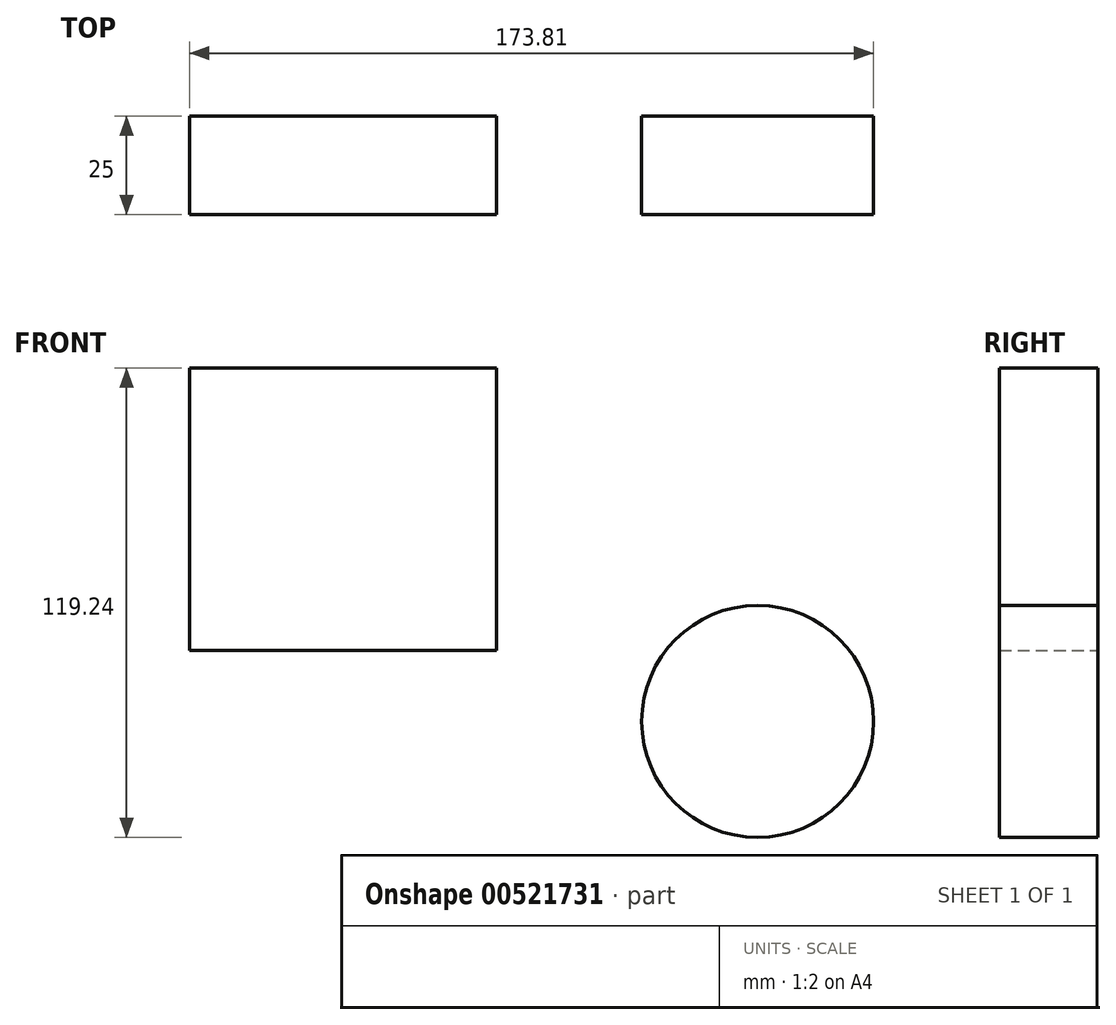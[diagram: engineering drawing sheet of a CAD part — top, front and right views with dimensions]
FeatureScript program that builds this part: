
annotation { "Feature Type Name" : "Feature", "Feature Type Description" : "" }
export const myFeature = defineFeature(function(context is Context, id is Id, definition is map)
    precondition{}
    {
        {
            var Q0;
            Q0=qCreatedBy(makeId("Front.planeOp"),FACE);
            var sketch = newSketch(context, id + "F0", { "sketchPlane" : qUnion([Q0])});
            skLineSegment(sketch, "E0.bottom", {"start": v(-105.01, 44.26) * mm, "end": v(-26.97, 44.26) * mm});
            skLineSegment(sketch, "E0.top", {"start": v(-105.01, -27.44) * mm, "end": v(-26.97, -27.44) * mm});
            skLineSegment(sketch, "E0.left", {"start": v(-105.01, 44.26) * mm, "end": v(-105.01, -27.44) * mm});
            skLineSegment(sketch, "E0.right", {"start": v(-26.97, 44.26) * mm, "end": v(-26.97, -27.44) * mm});
            skCircle(sketch, "E1", {"center": v(39.34, -45.53) * mm, "radius": 29.46 * mm});
            skSolve(sketch);
        }
        {
            var Q0;
            Q0 = qSketchRegion(id + "F0", true);
            extrude(context, id + "F1", {"entities" : qUnion([Q0]), "depth" : 25 * mm, "offsetDistance" : 25 * mm});
        }
    });
